# Revit family: Power-MouldedCaseDevices-GEWISS-97MSS-SWITCH_DISCONNECTOR_250_3P
name_source: partatom
category: Apparecchi elettrici
revit_build: Autodesk Revit 2016 (Build: 20161004_0715(x64)
units: mm (PartAtom-declared; Revit-internal decimal feet)

## family parameters
Condiviso = No
Host = Muro
Mantenere orientamento annotazione = Sì
Numero OmniClass = 23.80.50.00
Punto di calcolo locali = Sì
Quota connettore circolare = Usa diametro
Sempre verticale = Sì
Taglio con vuoti quando caricato = No
Tipo di parte = Normale
Titolo OmniClass = Terminals for Power Supply

## types (1)
- GW97729 - SWITCH DISCONNECTOR MSS 250 3P 250A
    Catalogue = POWER
    Catalogue Range = 97 MSS
    Descrizione = SWITCH DISCONNECTOR MSS 250 3P 250A
    EAN code = 8011564211490
    GW - Codice Electrocod = 150
    IDF = b491c06c-6c49-41eb-bcf7-d1657a9909a9
    IDT = 995b30e6-bc12-40ad-beca-8cd5aff8f7e2
    Immagine tipo = GW97729.jpg
    Label = MSS 250
    Modello = GW97729
    No. of poles = 3P
    Number of poles = 3P
    Produttore = GEWISS S.p.A.
    Rated current (In) = 250A
    Rated current: = 250A
    Rated voltage = 400V
    SEO = Disconnector
    Technical sheet = https://www.gewiss.com
    URL = https://www.gewiss.com
    Version file RFA = 18.0
